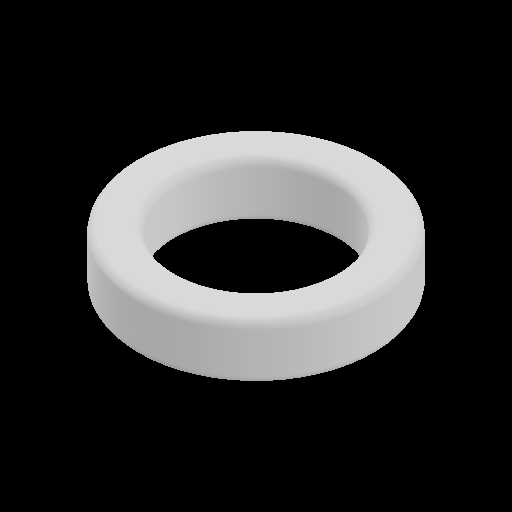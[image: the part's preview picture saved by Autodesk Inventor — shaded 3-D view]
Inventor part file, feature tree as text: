
AUTODESK INVENTOR PART (.ipt)
format: ipt  version: 2023 (Build 270158000, 158)  size: 116,736 bytes
history: native  units: mm
features: fillet x1
ambient origin geometry x8: Origin, YZ Plane, XZ Plane, XY Plane, X Axis, Y Axis, Z Axis, Center Point
bodies: Solid1 (feature_tree)
feature tree (1):
  fillet  "Fillet1"  [1 undecoded]
note: 1 required parameter value undecoded (feature->parameter linkage not recoverable at this tier; creation-order binding heuristic only, values carry confidence <= 0.55)
